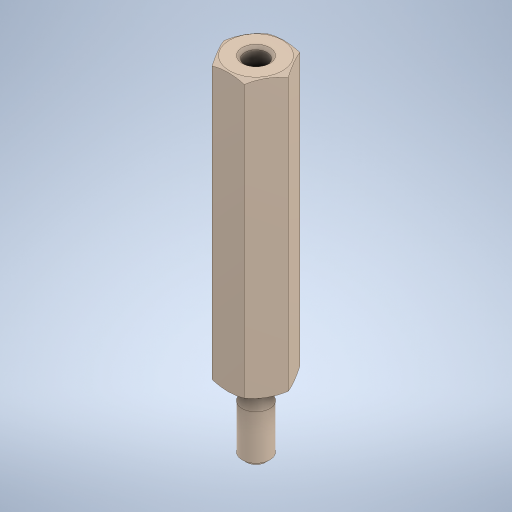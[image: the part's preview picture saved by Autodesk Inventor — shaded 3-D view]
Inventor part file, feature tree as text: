
AUTODESK INVENTOR PART (.ipt)
format: ipt  version: 2024 (Build 280153000, 153)  size: 284,672 bytes
history: native  units: mm
features: hole x1
ambient origin geometry x8: Origin, YZ Plane, XZ Plane, XY Plane, X Axis, Y Axis, Z Axis, Center Point
bodies: Solid1 (feature_tree)
feature tree (1):
  hole  "Bohrung1"  [1 undecoded]
note: 1 required parameter value undecoded (feature->parameter linkage not recoverable at this tier; creation-order binding heuristic only, values carry confidence <= 0.55)
